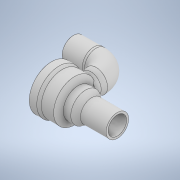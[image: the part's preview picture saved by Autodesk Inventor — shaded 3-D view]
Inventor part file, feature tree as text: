
AUTODESK INVENTOR PART (.ipt)
format: ipt  version: 2020 (Build 240168000, 168)  size: 891,904 bytes
history: native  units: mm
features: sketch x14, revolve x7, extrude x6, plane x5, other x3, projected_geometry x2, thread x1, helix x1
ambient origin geometry x8: Origin, YZ Plane, XZ Plane, XY Plane, X Axis, Y Axis, Z Axis, Center Point
bodies: Solid1 (feature_tree), Solid2 (feature_tree)
feature tree (39):
  revolve  "Revolution1"  [1 undecoded]
  thread  "Thread1"  [1 undecoded]
  revolve  "Revolution2"  [1 undecoded]
  helix  "Coil1"  [1 undecoded]
  plane  "Work Plane1"
  extrude  "Extrusion1"  Depth=17.95mm
  extrude  "Extrusion2"  Depth=16.0mm
  plane  "Work Plane2"
  extrude  "Extrusion3"  Depth=20.5mm
  extrude  "Extrusion4"  TaperAngle=0.0deg  [1 undecoded]
  extrude  "Extrusion5"  Depth=21.8mm
  extrude  "Extrusion6"  Depth=10.5mm
  other  "Work Axis1"
  revolve  "Revolution3"  Angle=90.0deg
  revolve  "Revolution4"  [1 undecoded]
  plane  "Work Plane3"
  revolve  "Revolution5"  [1 undecoded]
  plane  "Work Plane4"
  plane  "Work Plane5"
  other  "Bend Part1"
  other  "Work Axis3"
  revolve  "Revolution6"  [1 undecoded]
  revolve  "Revolution7"  [1 undecoded]
  sketch  "Sketch1"  dims[d0=25.0mm d1=11.0mm d2=11.25mm]
  sketch  "Sketch2"  dims[d3=9.0mm d10=20.5mm d12=120.0deg]
  sketch  "Sketch3"  dims[d13=0.0mm d14=17.95mm]
  sketch  "Sketch4"  dims[d15=17.95mm d16=16.0mm]
  sketch  "Sketch5"  dims[d17=17.0mm d18=20.5mm]
  sketch  "Sketch6"  dims[d19=12.0mm d20=0.0mm]
  sketch  "Sketch7"  dims[d21=20.0mm d23=21.8mm]
  sketch  "Sketch8"  dims[d24=3.0mm d25=10.5mm]
  sketch  "Sketch9"  dims[d26=0.0mm d27=90.0deg]
  sketch  "Sketch11"  dims[d28=2.0mm d29=2.0mm]
  projected_geometry  "Projected Loop1"
  sketch  "Sketch13"  dims[d30=2.0mm d31=7.0mm d32=1.5mm]
  projected_geometry  "Projected Loop2"
  sketch  "Sketch16"  dims[d33=9.599311mm d34=0.240125mm d35=0.240125mm d38=1.5mm]
  sketch  "Sketch18"  dims[d40=9.599311mm d42=0.0mm]
  sketch  "Sketch20"  dims[d43=1.5015mm d44=10.0mm d45=10.0mm d46=0.0mm d47=0.0mm d48=0.0mm d49=0.0mm d50=0.0mm d51=-15.164mm d52=3.5mm d53=8.0mm d54=2.0mm d55=2.0mm d56=3.0mm d57=0.0mm d58=6.5mm d59=2.0mm d60=0.0mm d61=20.5mm d63=12.5mm d64=7.0mm d65=10.0mm d66=0.0mm d67=15.0mm d68=7.0mm d69=0.0mm d70=3.5mm d71=7.0mm d72=3.5mm d73=20.0mm d74=2.0mm d75=0.0mm d76=2.5mm d77=0.0mm d78=1.0mm d79=0.0mm d81=9.0mm d82=11.25mm d83=11.25mm d84=10.0mm d85=0.0mm d86=90.0deg d87=5.0mm d88=90.0deg d89=90.0deg d90=-50.0mm d94=5.0mm d95=90.0deg d96=27.5mm d97=13.962634mm d98=20.0mm d99=20.0mm d100=11.0mm d101=13.962634mm d91=0.5mm d92=0.872665mm]
note: 9 required parameter values undecoded (feature->parameter linkage not recoverable at this tier; creation-order binding heuristic only, values carry confidence <= 0.55)